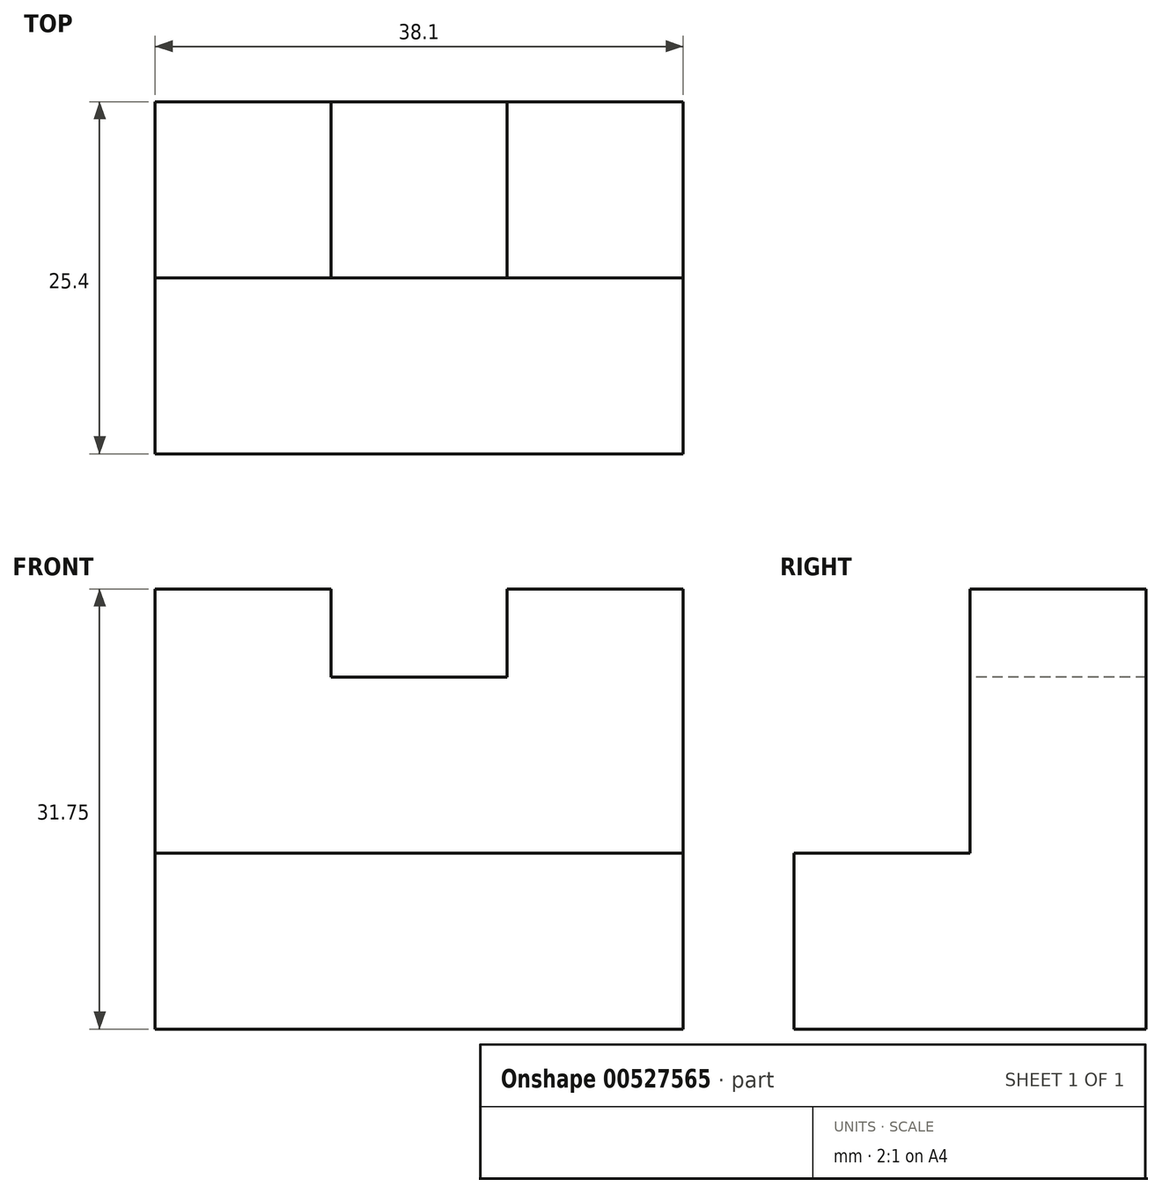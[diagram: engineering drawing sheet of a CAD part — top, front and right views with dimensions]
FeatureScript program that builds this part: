
annotation { "Feature Type Name" : "Feature", "Feature Type Description" : "" }
export const myFeature = defineFeature(function(context is Context, id is Id, definition is map)
    precondition{}
    {
        {
            var Q0;
            Q0=qCreatedBy(makeId("Right.planeOp"),FACE);
            var sketch = newSketch(context, id + "F0", { "sketchPlane" : qUnion([Q0])});
            skLineSegment(sketch, "E0", {"start": v(0, 0) * mm, "end": v(25.4, 0) * mm});
            skLineSegment(sketch, "E1", {"start": v(25.4, 0) * mm, "end": v(25.4, 31.75) * mm});
            skLineSegment(sketch, "E2", {"start": v(25.4, 31.75) * mm, "end": v(12.7, 31.75) * mm});
            skLineSegment(sketch, "E3", {"start": v(12.7, 31.75) * mm, "end": v(12.7, 12.7) * mm});
            skLineSegment(sketch, "E4", {"start": v(12.7, 12.7) * mm, "end": v(0, 12.7) * mm});
            skLineSegment(sketch, "E5", {"start": v(0, 12.7) * mm, "end": v(0, 0) * mm});
            skSolve(sketch);
        }
        {
            var Q0;
            Q0=makeQuery(id+"F0.imprint","IMPRINT",FACE,{"disambiguationData":[TD([[makeQuery(id+"F0.imprint","IMPRINT",EDGE,{"derivedFrom":sQuery(id+"F0.wireOp",EDGE,"E0")}),1.0]])]});
            extrude(context, id + "F1", {"entities" : qUnion([Q0]), "oppositeDirection" : true, "depth" : 38.1 * mm, "offsetDistance" : 25.4 * mm});
        }
        {
            var Q0;
            Q0=makeQuery(id+"F1.opExtrude","SWEPT_FACE",FACE,{"disambiguationData":[OSD([sQuery(id+"F0.wireOp",EDGE,"E2")])]});
            var sketch = newSketch(context, id + "F2", { "sketchPlane" : qUnion([Q0])});
            skLineSegment(sketch, "E6", {"start": v(-25.4, 25.4) * mm, "end": v(-25.4, 12.7) * mm});
            skLineSegment(sketch, "E7", {"start": v(-12.7, 25.4) * mm, "end": v(-12.7, 12.7) * mm});
            skSolve(sketch);
        }
        {
            var Q0;
            {var subQ0=sQuery(id+"F2.wireOp",EDGE,"E6");Q0=makeQuery(id+"F2.imprint","IMPRINT",FACE,{"disambiguationData":[TD([[makeQuery(id+"F2.imprint","IMPRINT",EDGE,{"derivedFrom":subQ0}),1.0]])]});}
            extrude(context, id + "F3", {"entities" : qUnion([Q0]), "operationType" : NewBodyOperationType.REMOVE, "oppositeDirection" : true, "depth" : 6.35 * mm, "offsetDistance" : 25.4 * mm});
        }
    });
